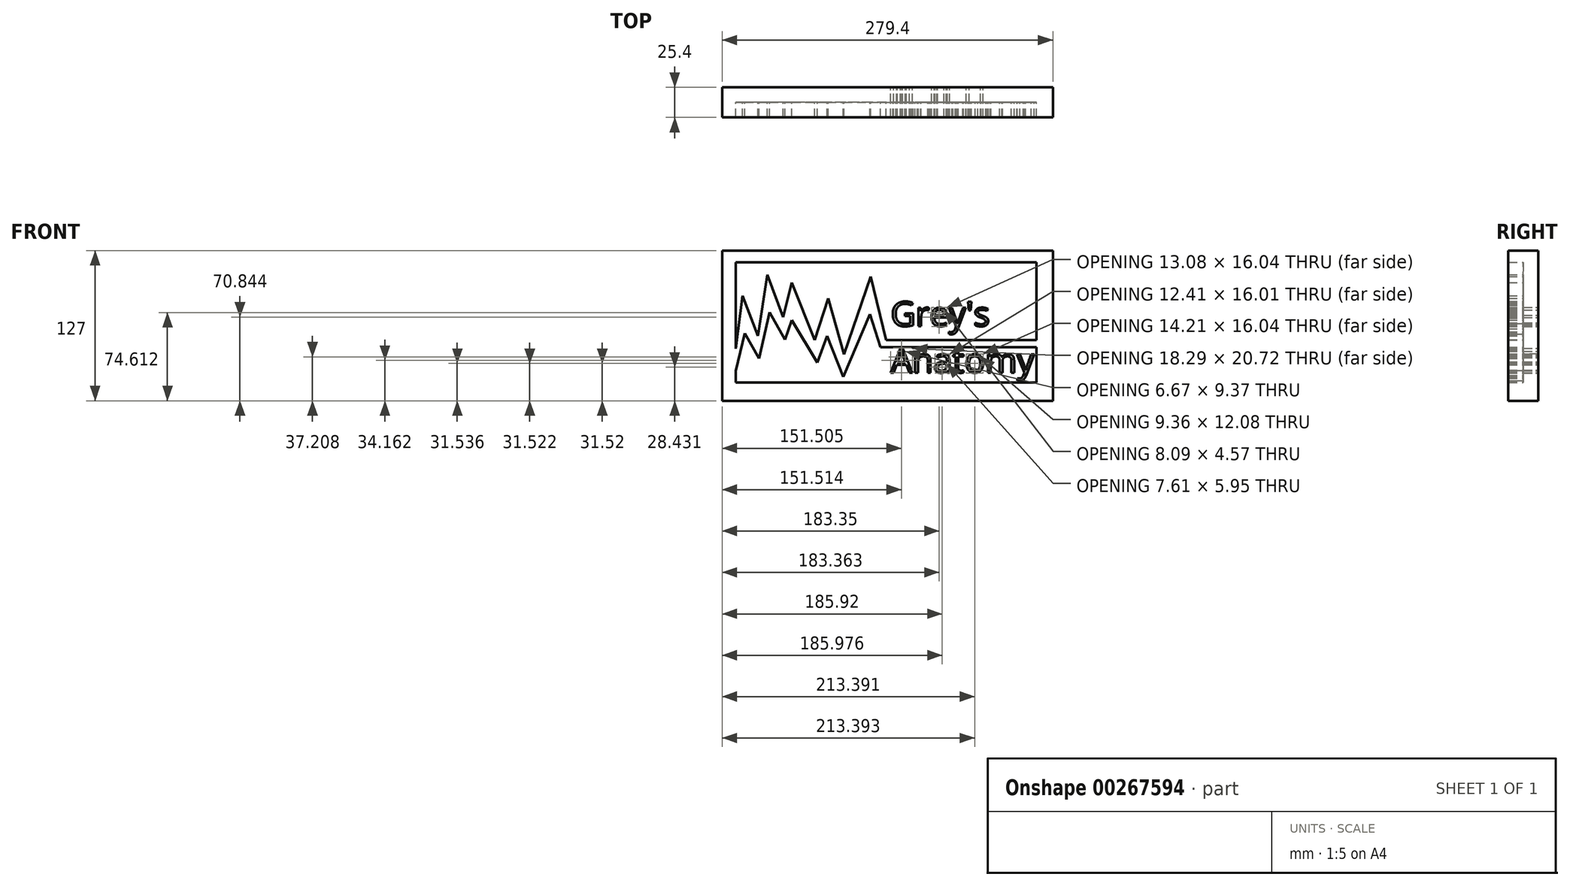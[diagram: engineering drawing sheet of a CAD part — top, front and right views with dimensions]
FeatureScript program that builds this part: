
annotation { "Feature Type Name" : "Feature", "Feature Type Description" : "" }
export const myFeature = defineFeature(function(context is Context, id is Id, definition is map)
    precondition{}
    {
        {
            var Q0;
            Q0=qCreatedBy(makeId("Front.planeOp"),FACE);
            var sketch = newSketch(context, id + "F0", { "sketchPlane" : qUnion([Q0])});
            skLineSegment(sketch, "E0", {"start": v(-132.22, 53.92) * mm, "end": v(121.78, 53.92) * mm});
            skLineSegment(sketch, "E1", {"start": v(121.78, 53.92) * mm, "end": v(121.78, -47.68) * mm});
            skLineSegment(sketch, "E2", {"start": v(121.78, -47.68) * mm, "end": v(-132.22, -47.68) * mm});
            skLineSegment(sketch, "E3", {"start": v(-132.22, -47.68) * mm, "end": v(-132.22, 53.92) * mm});
            skLineSegment(sketch, "E4", {"start": v(121.78, 0) * mm, "end": v(-1.3, 0) * mm});
            skText(sketch, "E5", { "text": "Grey\'s \nAnatomy", "fontName": "OpenSans-Regular.ttf"});
            skLineSegment(sketch, "E6", {"start": v(121.78, -11.81) * mm, "end": v(-5.22, -11.81) * mm});
            skPoint(sketch, "E6.endSnap0", {"position": v(-5.22, -47.68) * mm});
            skLineSegment(sketch, "E7", {"start": v(-5.22, -11.81) * mm, "end": v(-18.18, 42) * mm});
            skLineSegment(sketch, "E8", {"start": v(-18.18, 42) * mm, "end": v(-40.67, -23.96) * mm});
            skLineSegment(sketch, "E9", {"start": v(-40.67, -23.96) * mm, "end": v(-54.1, 23.5) * mm});
            skLineSegment(sketch, "E10", {"start": v(-54.1, 23.5) * mm, "end": v(-65.53, -11.61) * mm});
            skLineSegment(sketch, "E11", {"start": v(-65.53, -11.61) * mm, "end": v(-84.87, 36.92) * mm});
            skLineSegment(sketch, "E12", {"start": v(-84.87, 36.92) * mm, "end": v(-91.97, 7.52) * mm});
            skLineSegment(sketch, "E13", {"start": v(-91.97, 7.52) * mm, "end": v(-105.38, 43.43) * mm});
            skLineSegment(sketch, "E14", {"start": v(-105.38, 43.43) * mm, "end": v(-113.28, -8.26) * mm});
            skLineSegment(sketch, "E15", {"start": v(-113.28, -8.26) * mm, "end": v(-126.3, 25.67) * mm});
            skLineSegment(sketch, "E16", {"start": v(-126.3, 25.67) * mm, "end": v(-132.22, -18.91) * mm});
            skLineSegment(sketch, "E17.bottom", {"start": v(-143.66, 63.9) * mm, "end": v(135.74, 63.9) * mm});
            skLineSegment(sketch, "E17.top", {"start": v(-143.66, -63.1) * mm, "end": v(135.74, -63.1) * mm});
            skLineSegment(sketch, "E17.left", {"start": v(-143.66, 63.9) * mm, "end": v(-143.66, -63.1) * mm});
            skLineSegment(sketch, "E17.right", {"start": v(135.74, 63.9) * mm, "end": v(135.74, -63.1) * mm});
            skLineSegment(sketch, "E18", {"start": v(-132.22, -37.92) * mm, "end": v(-124.65, -6.03) * mm});
            skLineSegment(sketch, "E19", {"start": v(-124.65, -6.03) * mm, "end": v(-112.43, -27.31) * mm});
            skLineSegment(sketch, "E20", {"start": v(-112.43, -27.31) * mm, "end": v(-103.66, 11.68) * mm});
            skLineSegment(sketch, "E21", {"start": v(-103.66, 11.68) * mm, "end": v(-90.45, -11.47) * mm});
            skLineSegment(sketch, "E22", {"start": v(-90.45, -11.47) * mm, "end": v(-84.81, 5.17) * mm});
            skLineSegment(sketch, "E23", {"start": v(-84.81, 5.17) * mm, "end": v(-63.2, -30.66) * mm});
            skLineSegment(sketch, "E24", {"start": v(-63.2, -30.66) * mm, "end": v(-54.96, -8.23) * mm});
            skLineSegment(sketch, "E25", {"start": v(-54.96, -8.23) * mm, "end": v(-41.17, -43) * mm});
            skLineSegment(sketch, "E26", {"start": v(-41.17, -43) * mm, "end": v(-18.93, 10.25) * mm});
            skLineSegment(sketch, "E27", {"start": v(-18.93, 10.25) * mm, "end": v(-9.84, -17.94) * mm});
            skLineSegment(sketch, "E28", {"start": v(-9.84, -17.94) * mm, "end": v(121.78, -17.94) * mm});
            const initialGuessF0  = {"E5": [-0.0013, 0, 1, 0, 0.02081]};
            skSetInitialGuess(sketch, initialGuessF0);
            skSolve(sketch);
        }
        {
            var Q0;
            {var subQ3=sQuery(id+"F0.wireOp",EDGE,"E0");Q0=makeQuery(id+"F0.imprint","IMPRINT",FACE,{"disambiguationData":[TD([[makeQuery(id+"F0.imprint","IMPRINT",EDGE,{"derivedFrom":subQ3}),1.0]])]});}
            extrude(context, id + "F1", {"entities" : qUnion([Q0]), "depth" : 25.4 * mm});
        }
        {
            var Q0;
            {var subQ26=sQuery(id+"F0.wireOp",EDGE,"E0");Q0=makeQuery(id+"F0.imprint","IMPRINT",FACE,{"disambiguationData":[TD([[makeQuery(id+"F0.imprint","IMPRINT",EDGE,{"derivedFrom":subQ26}),-1.0]])]});}
            var Q1;
            {var subQ0=sQuery(id+"F0.wireOp",EDGE,"E2");Q1=makeQuery(id+"F0.imprint","IMPRINT",FACE,{"disambiguationData":[TD([[makeQuery(id+"F0.imprint","IMPRINT",EDGE,{"derivedFrom":subQ0}),-1.0]])]});}
            var Q2;
            Q2=makeQuery(id+"F0.imprint","IMPRINT",FACE,{"disambiguationData":[TD([[makeQuery(id+"F0.imprint","IMPRINT",EDGE,{"derivedFrom":sQuery(id+"F0.wireOp",EDGE,"E5.sketch_text.stroke-105")}),1.0]])]});
            var Q3;
            Q3=makeQuery(id+"F0.imprint","IMPRINT",FACE,{"disambiguationData":[TD([[makeQuery(id+"F0.imprint","IMPRINT",EDGE,{"derivedFrom":sQuery(id+"F0.wireOp",EDGE,"E5.sketch_text.stroke-146")}),1.0]])]});
            var Q4;
            Q4=makeQuery(id+"F0.imprint","IMPRINT",FACE,{"disambiguationData":[TD([[makeQuery(id+"F0.imprint","IMPRINT",EDGE,{"derivedFrom":sQuery(id+"F0.wireOp",EDGE,"E5.sketch_text.stroke-182")}),1.0]])]});
            var Q5;
            Q5=makeQuery(id+"F0.imprint","IMPRINT",FACE,{"disambiguationData":[TD([[makeQuery(id+"F0.imprint","IMPRINT",EDGE,{"derivedFrom":sQuery(id+"F0.wireOp",EDGE,"E5.sketch_text.stroke-47")}),1.0]])]});
            extrude(context, id + "F2", {"entities" : qUnion([Q0, Q1, Q2, Q3, Q4, Q5]), "operationType" : NewBodyOperationType.ADD, "depth" : 12.7 * mm});
        }
        {
            var Q0;
            {var subQ2=sQuery(id+"F0.wireOp",EDGE,"E6");Q0=makeQuery(id+"F0.imprint","IMPRINT",FACE,{"disambiguationData":[TD([[makeQuery(id+"F0.imprint","IMPRINT",EDGE,{"derivedFrom":subQ2}),1.0]])]});}
            extrude(context, id + "F3", {"entities" : qUnion([Q0]), "operationType" : NewBodyOperationType.ADD, "depth" : 25.4 * mm});
        }
        {
            var Q0;
            Q0=makeQuery(id+"F0.imprint","IMPRINT",FACE,{"disambiguationData":[TD([[makeQuery(id+"F0.imprint","IMPRINT",EDGE,{"derivedFrom":sQuery(id+"F0.wireOp",EDGE,"E5.sketch_text.stroke-0")}),-1.0]])]});
            var Q1;
            {var subQ5=sQuery(id+"F0.wireOp",EDGE,"E5.sketch_text.stroke-3");Q1=makeQuery(id+"F0.imprint","IMPRINT",FACE,{"disambiguationData":[TD([[makeQuery(id+"F0.imprint","IMPRINT",EDGE,{"derivedFrom":subQ5}),-1.0]])]});}
            extrude(context, id + "F4", {"entities" : qUnion([Q0, Q1]), "operationType" : NewBodyOperationType.ADD, "depth" : 25.4 * mm});
        }
        {
            var Q0;
            Q0=makeQuery(id+"F0.imprint","IMPRINT",FACE,{"disambiguationData":[TD([[makeQuery(id+"F0.imprint","IMPRINT",EDGE,{"derivedFrom":sQuery(id+"F0.wireOp",EDGE,"E5.sketch_text.stroke-20")}),-1.0]])]});
            extrude(context, id + "F5", {"entities" : qUnion([Q0]), "operationType" : NewBodyOperationType.ADD, "depth" : 25.4 * mm});
        }
        {
            var Q0;
            {var subQ6=sQuery(id+"F0.wireOp",EDGE,"E5.sketch_text.stroke-34");Q0=makeQuery(id+"F0.imprint","IMPRINT",FACE,{"disambiguationData":[TD([[makeQuery(id+"F0.imprint","IMPRINT",EDGE,{"derivedFrom":subQ6}),-1.0]])]});}
            var Q1;
            {var subQ5=sQuery(id+"F0.wireOp",EDGE,"E5.sketch_text.stroke-46");Q1=makeQuery(id+"F0.imprint","IMPRINT",FACE,{"disambiguationData":[TD([[makeQuery(id+"F0.imprint","IMPRINT",EDGE,{"derivedFrom":subQ5}),-1.0]])]});}
            extrude(context, id + "F6", {"entities" : qUnion([Q0, Q1]), "depth" : 25.4 * mm});
        }
        {
            var Q0;
            {var subQ0=sQuery(id+"F0.wireOp",EDGE,"E5.sketch_text.stroke-52");Q0=makeQuery(id+"F0.imprint","IMPRINT",FACE,{"disambiguationData":[TD([[makeQuery(id+"F0.imprint","IMPRINT",EDGE,{"derivedFrom":subQ0}),-1.0]])]});}
            var Q1;
            {var subQ5=sQuery(id+"F0.wireOp",EDGE,"E5.sketch_text.stroke-60");Q1=makeQuery(id+"F0.imprint","IMPRINT",FACE,{"disambiguationData":[TD([[makeQuery(id+"F0.imprint","IMPRINT",EDGE,{"derivedFrom":subQ5}),-1.0]])]});}
            extrude(context, id + "F7", {"entities" : qUnion([Q0, Q1]), "operationType" : NewBodyOperationType.ADD, "depth" : 25.4 * mm});
        }
        {
            var Q0;
            Q0=makeQuery(id+"F0.imprint","IMPRINT",FACE,{"disambiguationData":[TD([[makeQuery(id+"F0.imprint","IMPRINT",EDGE,{"derivedFrom":sQuery(id+"F0.wireOp",EDGE,"E5.sketch_text.stroke-68")}),-1.0]])]});
            extrude(context, id + "F8", {"entities" : qUnion([Q0]), "operationType" : NewBodyOperationType.ADD, "depth" : 25.4 * mm});
        }
        {
            var Q0;
            {var subQ1=sQuery(id+"F0.wireOp",EDGE,"E5.sketch_text.stroke-72");Q0=makeQuery(id+"F0.imprint","IMPRINT",FACE,{"disambiguationData":[TD([[makeQuery(id+"F0.imprint","IMPRINT",EDGE,{"derivedFrom":subQ1}),-1.0]])]});}
            var Q1;
            {var subQ0=sQuery(id+"F0.wireOp",EDGE,"E5.sketch_text.stroke-73");var subQ1=sQuery(id+"F0.wireOp",EDGE,"E4");var subQ2=makeQuery(id+"F0.imprint","INTERSECT",VERTEX,{"derivedFrom":[subQ1,subQ0]});Q1=makeQuery(id+"F0.imprint","IMPRINT",FACE,{"disambiguationData":[TD([[makeQuery(id+"F0.imprint","IMPRINT",EDGE,{"disambiguationData":[TD([[subQ2,-1.0]])],"derivedFrom":subQ1}),1.0]])]});}
            extrude(context, id + "F9", {"entities" : qUnion([Q0, Q1]), "operationType" : NewBodyOperationType.ADD, "depth" : 25.4 * mm});
        }
        {
            var Q0;
            Q0=makeQuery(id+"F0.imprint","IMPRINT",FACE,{"disambiguationData":[TD([[makeQuery(id+"F0.imprint","IMPRINT",EDGE,{"derivedFrom":sQuery(id+"F0.wireOp",EDGE,"E5.sketch_text.stroke-97")}),-1.0]])]});
            extrude(context, id + "F10", {"entities" : qUnion([Q0]), "depth" : 25.4 * mm});
        }
        {
            var Q0;
            Q0=makeQuery(id+"F0.imprint","IMPRINT",FACE,{"disambiguationData":[TD([[makeQuery(id+"F0.imprint","IMPRINT",EDGE,{"derivedFrom":sQuery(id+"F0.wireOp",EDGE,"E5.sketch_text.stroke-110")}),-1.0]])]});
            extrude(context, id + "F11", {"entities" : qUnion([Q0]), "operationType" : NewBodyOperationType.ADD, "depth" : 25.4 * mm});
        }
        {
            var Q0;
            Q0=makeQuery(id+"F0.imprint","IMPRINT",FACE,{"disambiguationData":[TD([[makeQuery(id+"F0.imprint","IMPRINT",EDGE,{"derivedFrom":sQuery(id+"F0.wireOp",EDGE,"E5.sketch_text.stroke-127")}),-1.0]])]});
            extrude(context, id + "F12", {"entities" : qUnion([Q0]), "depth" : 25.4 * mm});
        }
        {
            var Q0;
            Q0=makeQuery(id+"F0.imprint","IMPRINT",FACE,{"disambiguationData":[TD([[makeQuery(id+"F0.imprint","IMPRINT",EDGE,{"derivedFrom":sQuery(id+"F0.wireOp",EDGE,"E5.sketch_text.stroke-154")}),-1.0]])]});
            extrude(context, id + "F13", {"entities" : qUnion([Q0]), "operationType" : NewBodyOperationType.ADD, "depth" : 25.4 * mm});
        }
        {
            var Q0;
            Q0=makeQuery(id+"F0.imprint","IMPRINT",FACE,{"disambiguationData":[TD([[makeQuery(id+"F0.imprint","IMPRINT",EDGE,{"derivedFrom":sQuery(id+"F0.wireOp",EDGE,"E5.sketch_text.stroke-173")}),-1.0]])]});
            extrude(context, id + "F14", {"entities" : qUnion([Q0]), "depth" : 25.4 * mm});
        }
        {
            var Q0;
            Q0=makeQuery(id+"F0.imprint","IMPRINT",FACE,{"disambiguationData":[TD([[makeQuery(id+"F0.imprint","IMPRINT",EDGE,{"derivedFrom":sQuery(id+"F0.wireOp",EDGE,"E5.sketch_text.stroke-190")}),-1.0]])]});
            extrude(context, id + "F15", {"entities" : qUnion([Q0]), "operationType" : NewBodyOperationType.ADD, "depth" : 25.4 * mm});
        }
        {
            var Q0;
            Q0=makeQuery(id+"F0.imprint","IMPRINT",FACE,{"disambiguationData":[TD([[makeQuery(id+"F0.imprint","IMPRINT",EDGE,{"derivedFrom":sQuery(id+"F0.wireOp",EDGE,"E5.sketch_text.stroke-218")}),-1.0]])]});
            extrude(context, id + "F16", {"entities" : qUnion([Q0]), "operationType" : NewBodyOperationType.ADD, "depth" : 25.4 * mm});
        }
    });
